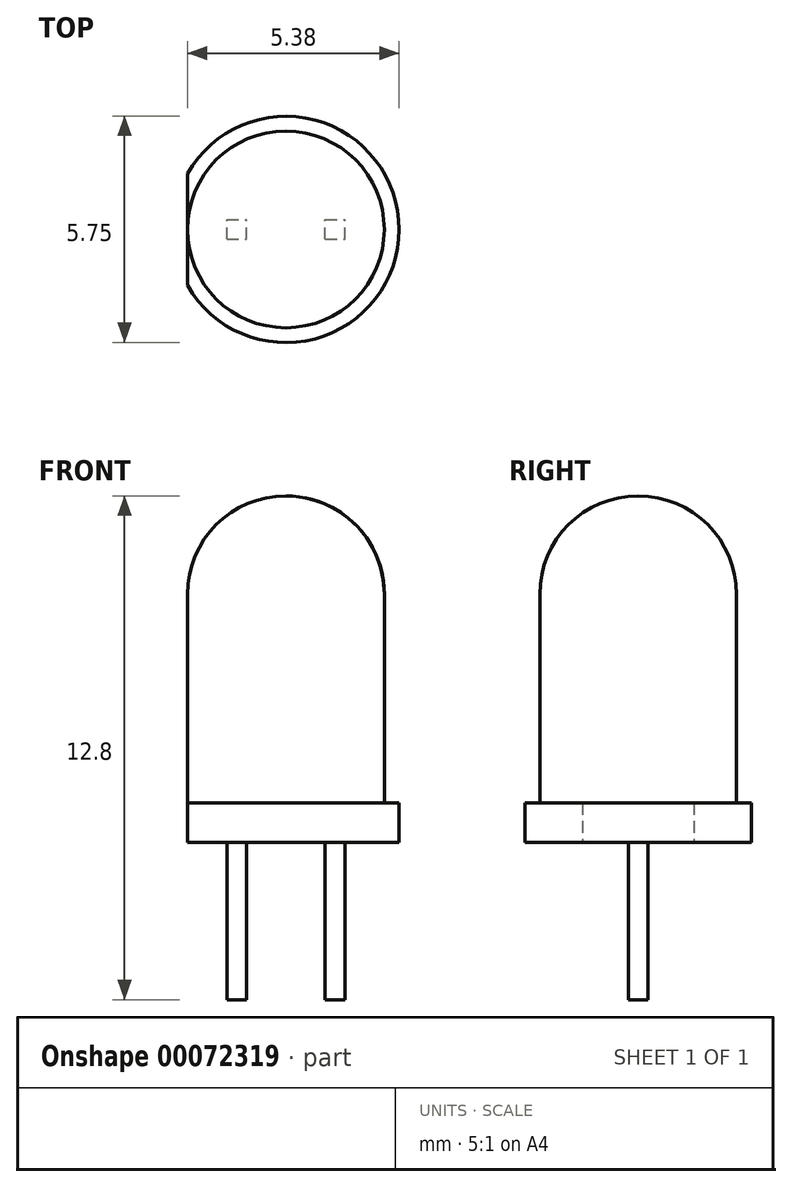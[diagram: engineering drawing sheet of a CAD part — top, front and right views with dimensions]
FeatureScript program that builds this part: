
annotation { "Feature Type Name" : "Feature", "Feature Type Description" : "" }
export const myFeature = defineFeature(function(context is Context, id is Id, definition is map)
    precondition{}
    {
        {
            var Q0;
            Q0=qCreatedBy(makeId("Top.planeOp"),FACE);
            var sketch = newSketch(context, id + "F0", { "sketchPlane" : qUnion([Q0])});
            skCircle(sketch, "E0", {"center": v(0, 0) * mm, "radius": 2.5 * mm});
            skArc(sketch, "E1", {"start": v(-2.5, -1.42) * mm, "mid": v(2.88, 0) * mm, "end": v(-2.5, 1.42) * mm});
            skLineSegment(sketch, "E2", {"start": v(-2.5, 1.42) * mm, "end": v(-2.5, -1.42) * mm});
            skSolve(sketch);
        }
        {
            var Q0;
            Q0=makeQuery(id+"F0.imprint","IMPRINT",FACE,{"disambiguationData":[TD([[makeQuery(id+"F0.imprint","IMPRINT",EDGE,{"derivedFrom":sQuery(id+"F0.wireOp",EDGE,"E0")}),1.0]])]});
            extrude(context, id + "F1", {"entities" : qUnion([Q0]), "depth" : 8.8 * mm});
        }
        {
            var Q0;
            Q0 = qSketchRegion(id + "F0", true);
            extrude(context, id + "F2", {"entities" : qUnion([Q0]), "operationType" : NewBodyOperationType.ADD, "depth" : 1 * mm});
        }
        {
            var Q0;
            Q0=makeQuery(id+"F1.opExtrude","CAP_EDGE",EDGE,{"disambiguationData":[OSD([sQuery(id+"F0.wireOp",EDGE,"E0")])],"isStart":false});
            fillet(context, id + "F3", {"entities" : qUnion([Q0]), "radius" : 2.5 * mm, "tangentPropagation" : true, "allowEdgeOverflow" : false});
        }
        {
            var Q0;
            Q0=makeQuery(id+"F2.boolean.opBoolean","MERGE",FACE,{"derivedFrom":[makeQuery(id+"F1.opExtrude","CAP_FACE",FACE,{"disambiguationData":[OSD([sQuery(id+"F0.wireOp",EDGE,"E0")])],"isStart":true}),makeQuery(id+"F2.opExtrude","CAP_FACE",FACE,{"disambiguationData":[OSD([sQuery(id+"F0.wireOp",EDGE,"E1"),sQuery(id+"F0.wireOp",EDGE,"E2")])],"isStart":true})]});
            var sketch = newSketch(context, id + "F4", { "sketchPlane" : qUnion([Q0])});
            skLineSegment(sketch, "E3.bottom", {"start": v(-1.5, 0.25) * mm, "end": v(-1, 0.25) * mm});
            skLineSegment(sketch, "E3.top", {"start": v(-1.5, -0.25) * mm, "end": v(-1, -0.25) * mm});
            skLineSegment(sketch, "E3.left", {"start": v(-1.5, 0.25) * mm, "end": v(-1.5, -0.25) * mm});
            skLineSegment(sketch, "E3.right", {"start": v(-1, 0.25) * mm, "end": v(-1, -0.25) * mm});
            skLineSegment(sketch, "E4.bottom", {"start": v(1, 0.25) * mm, "end": v(1.5, 0.25) * mm});
            skLineSegment(sketch, "E4.top", {"start": v(1, -0.25) * mm, "end": v(1.5, -0.25) * mm});
            skLineSegment(sketch, "E4.left", {"start": v(1, 0.25) * mm, "end": v(1, -0.25) * mm});
            skLineSegment(sketch, "E4.right", {"start": v(1.5, 0.25) * mm, "end": v(1.5, -0.25) * mm});
            skPoint(sketch, "E5", {"position": v(-1.5, 0) * mm});
            skLineSegment(sketch, "E6", {"start": v(-1, 0) * mm, "end": v(1, 0) * mm});
            skSolve(sketch);
        }
        {
            var Q0;
            Q0 = qSketchRegion(id + "F4", true);
            extrude(context, id + "F5", {"entities" : qUnion([Q0]), "operationType" : NewBodyOperationType.ADD, "depth" : 4 * mm});
        }
    });
